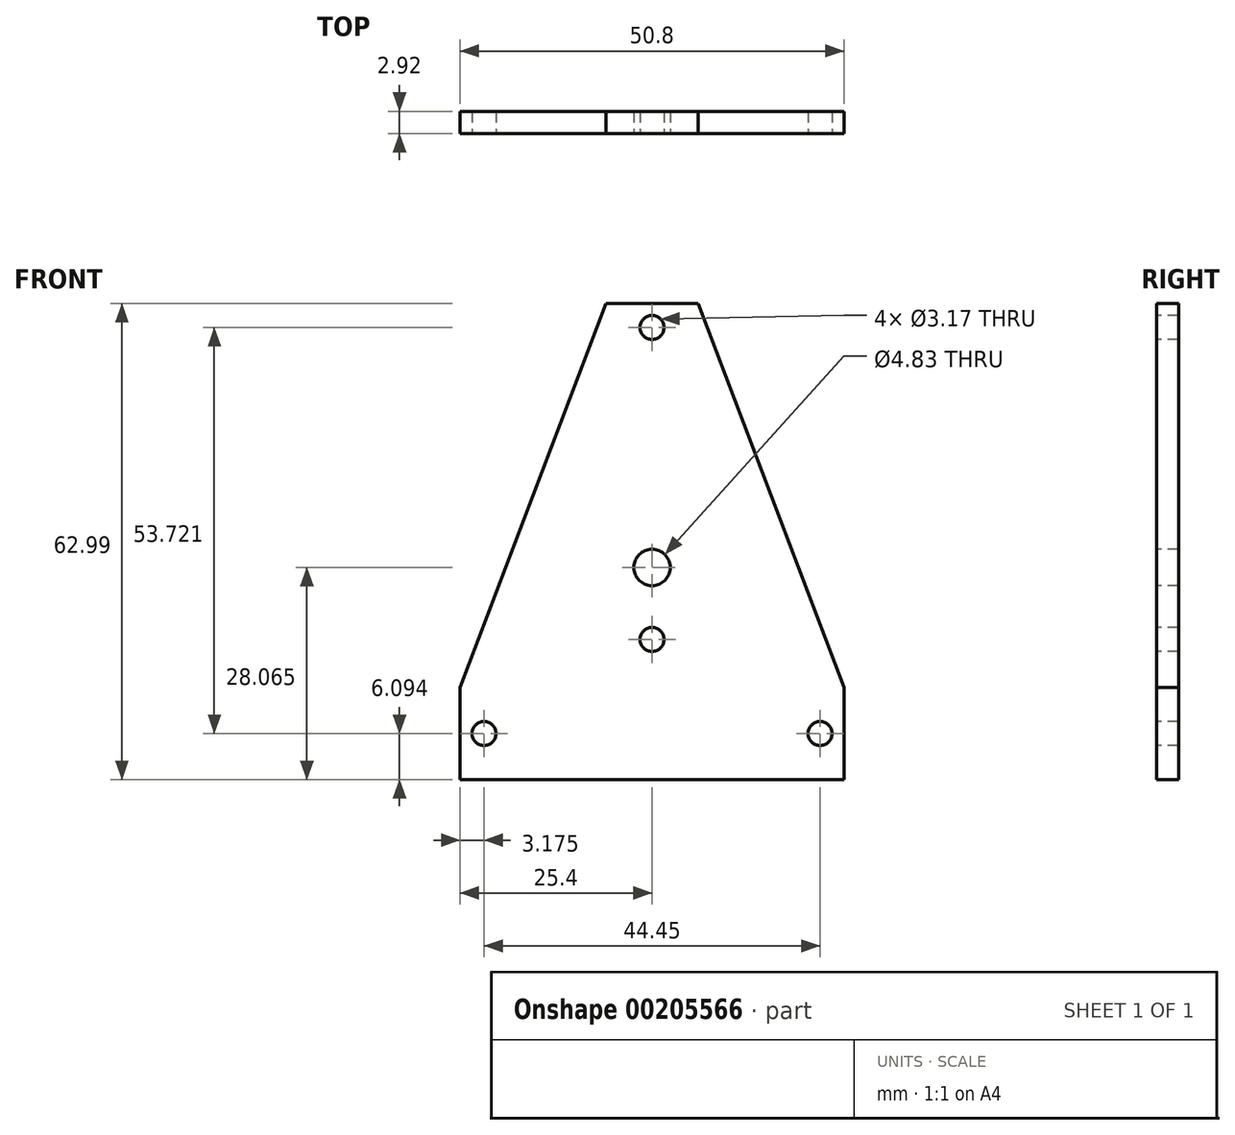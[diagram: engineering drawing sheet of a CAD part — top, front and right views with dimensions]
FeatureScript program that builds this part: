
annotation { "Feature Type Name" : "Feature", "Feature Type Description" : "" }
export const myFeature = defineFeature(function(context is Context, id is Id, definition is map)
    precondition{}
    {
        {
            var Q0;
            Q0=qCreatedBy(makeId("Front.planeOp"),FACE);
            var sketch = newSketch(context, id + "F0", { "sketchPlane" : qUnion([Q0])});
            skLineSegment(sketch, "E0", {"start": v(-25.4, 0) * mm, "end": v(-25.4, -12.2) * mm});
            skLineSegment(sketch, "E1", {"start": v(-25.4, -12.2) * mm, "end": v(25.4, -12.2) * mm});
            skLineSegment(sketch, "E2", {"start": v(25.4, -12.2) * mm, "end": v(25.4, 0) * mm});
            skLineSegment(sketch, "E3", {"start": v(25.4, 0) * mm, "end": v(6.1, 50.8) * mm});
            skLineSegment(sketch, "E4", {"start": v(6.1, 50.8) * mm, "end": v(-6.1, 50.8) * mm});
            skLineSegment(sketch, "E5", {"start": v(-6.1, 50.8) * mm, "end": v(-25.4, 0) * mm});
            skCircle(sketch, "E6", {"center": v(-22.23, -6.1) * mm, "radius": 1.59 * mm});
            skCircle(sketch, "E7", {"center": v(22.23, -6.1) * mm, "radius": 1.59 * mm});
            skCircle(sketch, "E8", {"center": v(0, 6.35) * mm, "radius": 1.59 * mm});
            skCircle(sketch, "E9", {"center": v(0, 47.63) * mm, "radius": 1.59 * mm});
            skCircle(sketch, "E10", {"center": v(0, 15.88) * mm, "radius": 2.41 * mm});
            skSolve(sketch);
        }
        {
            var Q0;
            Q0=qSketchRegion(id+"F0",true);
            extrude(context, id + "F1", {"entities" : qUnion([Q0]), "oppositeDirection" : true, "depth" : 2.92 * mm});
        }
    });
